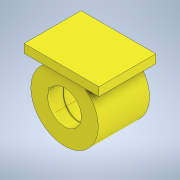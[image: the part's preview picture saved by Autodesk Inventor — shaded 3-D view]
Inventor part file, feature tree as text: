
AUTODESK INVENTOR PART (.ipt)
format: ipt  version: 2020 (Build 240168000, 168)  size: 264,192 bytes
history: native  units: in
note: dims shown in document units (in); Inventor stores cm internally (conversion verified against a paired STEP export)
features: sketch x3, extrude x2, plane x1, other x1, helix x1
ambient origin geometry x8: Origin, YZ Plane, XZ Plane, XY Plane, X Axis, Y Axis, Z Axis, Center Point
bodies: Solid1 (feature_tree)
feature tree (8):
  extrude  "Extrusion1"  Depth=1.9685in
  plane  "Work Plane1"
  extrude  "Extrusion2"  Depth=1.9685in
  sketch  "Sketch3"  dims[d7=0.1969in d8=1.0in d9=1.0in d10=1.1811in d11=0.0in d12=90.0deg d13=90.0deg d14=0.0in d15=0.0in]
  other  "Work Axis1"
  helix  "Coil1"  [1 undecoded]
  sketch  "Sketch1"  dims[d0=3.937in d1=1.9685in]
  sketch  "Sketch2"  dims[d2=3.0in d3=0.0in d4=1.9685in d5=0.5in d6=0.0in]
note: 1 required parameter value undecoded (feature->parameter linkage not recoverable at this tier; creation-order binding heuristic only, values carry confidence <= 0.55)
